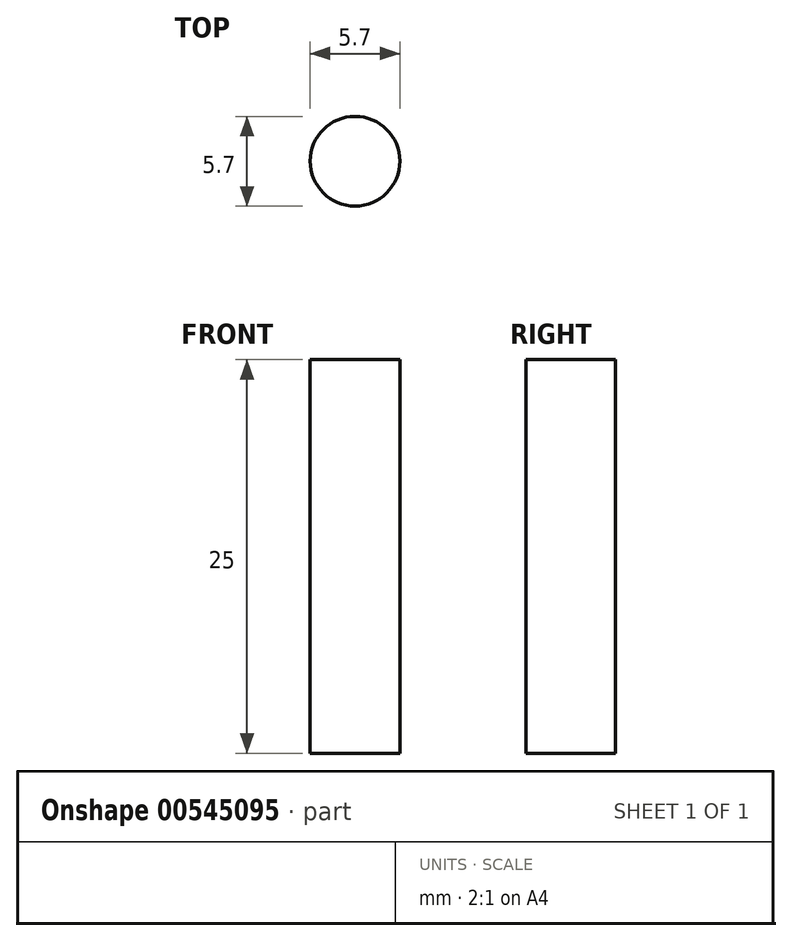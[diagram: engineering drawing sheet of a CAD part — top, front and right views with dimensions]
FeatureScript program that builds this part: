
annotation { "Feature Type Name" : "Feature", "Feature Type Description" : "" }
export const myFeature = defineFeature(function(context is Context, id is Id, definition is map)
    precondition{}
    {
        {
            var Q0;
            Q0=qCreatedBy(makeId("Top.planeOp"),FACE);
            var sketch = newSketch(context, id + "F0", { "sketchPlane" : qUnion([Q0])});
            skCircle(sketch, "E0", {"center": v(0, 0) * mm, "radius": 2.85 * mm});
            skSolve(sketch);
        }
        {
            var Q0;
            Q0 = qSketchRegion(id + "F0", true);
            extrude(context, id + "F1", {"entities" : qUnion([Q0]), "depth" : 25 * mm, "offsetDistance" : 25 * mm});
        }
    });
